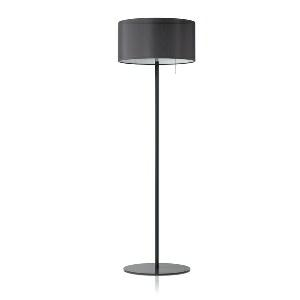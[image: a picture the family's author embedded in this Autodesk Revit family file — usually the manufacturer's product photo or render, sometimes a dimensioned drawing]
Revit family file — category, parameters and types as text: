
# Revit family: vivaa_free_-_vfs_7000_930_d_00812661_2909
name_source: partatom
category: Lighting Fixtures
units: mm (PartAtom-declared; Revit-internal decimal feet)

## family parameters
Cut with Voids When Loaded = No
Host = Face
Light Source = No
Part Type = Normal
Room Calculation Point = No
Round Connector Dimension = Use Diameter
Shared = No

## types (1)
- VIVAA.free - VFS 7000/930/D (1 x LED, 7200 lm, 3000K)
    Apparent Load = 79 VA
    Approval mark = CE
    CIE Flux Codes = 52 82 95 44 100
    Color Rendering = 90-100
    Color Temperature = 3000K
    Control Gear = Electronic ballast
    Default Elevation = 1800 mm
    Description = VFS 7000/930/D|Free-standing luminaire|light source:   Warm white   |work equipment: Electronic ballast|luminous flux: 7200 lm|light distribution: Direct/indirect|direct ratio: approx. 44 %|color rendering index (CRI): >= 90|chromaticity tolerance:  3 SDCM|technology: Continuously dimmable|operation: Pull cord|luminaire body|material: Polyethylene(PE)|surface: Untreated|colour: Anthracite|lamp cover: Polycarbonate (PC), Satine|tubular section|material: Steel tube|surface: Painted|Form: Tubular section upright|colour of tubular section: Anthracite grey|luminaire base|Form: Round (flat)|weight (net): approx. 12.3 kg|mains lead: 2.20 m Mains plug CEE 7/VII|Fastening: Floor standing base|glare control: Diffusor|luminance(L65): <= 1600 cd/m|unified glare rating(4H 8H): <=  16|
    Frequency = 50 Hz, 60 Hz
    Height = 250 mm
    Lamp = 1 x LED
    Lamp Light Flux = 7200 lm
    Lamp count = 1
    Length = 520 mm
    Luminous efficacy = 91 lm/W
    Manufacturer = Waldmann
    ModVariant = No
    Model = 00812661
    Mounting Place = Floor
    Mounting Type = Freestanding
    Number of Poles = 1
    OnlyDefault = Yes
    Power Factor = 1
    Product Name = VIVAA.free - VFS 7000/930/D
    Product group = Free standing luminaire
    ProductGroupID = 13
    Protection Class = Protection class I
    Protection Degree = Degree of protection
    RLX_Detail_Level = 1
    RLX_Emergency_Light_Flux = 0 lm
    RLX_Emergency_Type = 0
    RLX_Emergency_Type_DB = No
    RlxData = <blob elided: 19081 chars, md5=92bc47da>
    Socket = socket
    Standby Power = 0 W
    System Light Flux = 7200 lm
    System Power = 79 W
    Type Comments = Product without accessories
    Type Image = vivaa_free_metal_sw.jpg
    URL = http://relux.com
    VarID = ---
    Voltage = 230 V
    Voltage Range = 220-240 V
    Weight = 0.00 kg
    Width = 0 mm  [stored 0 ft]

note: [stored X ft] marks values corroborated as IEEE doubles in the binary element streams (Revit-internal decimal feet)

## geometry (parser evidence)
native form markers: Blend x4, Sweep x18
no freeform markers — native parametric forms only
